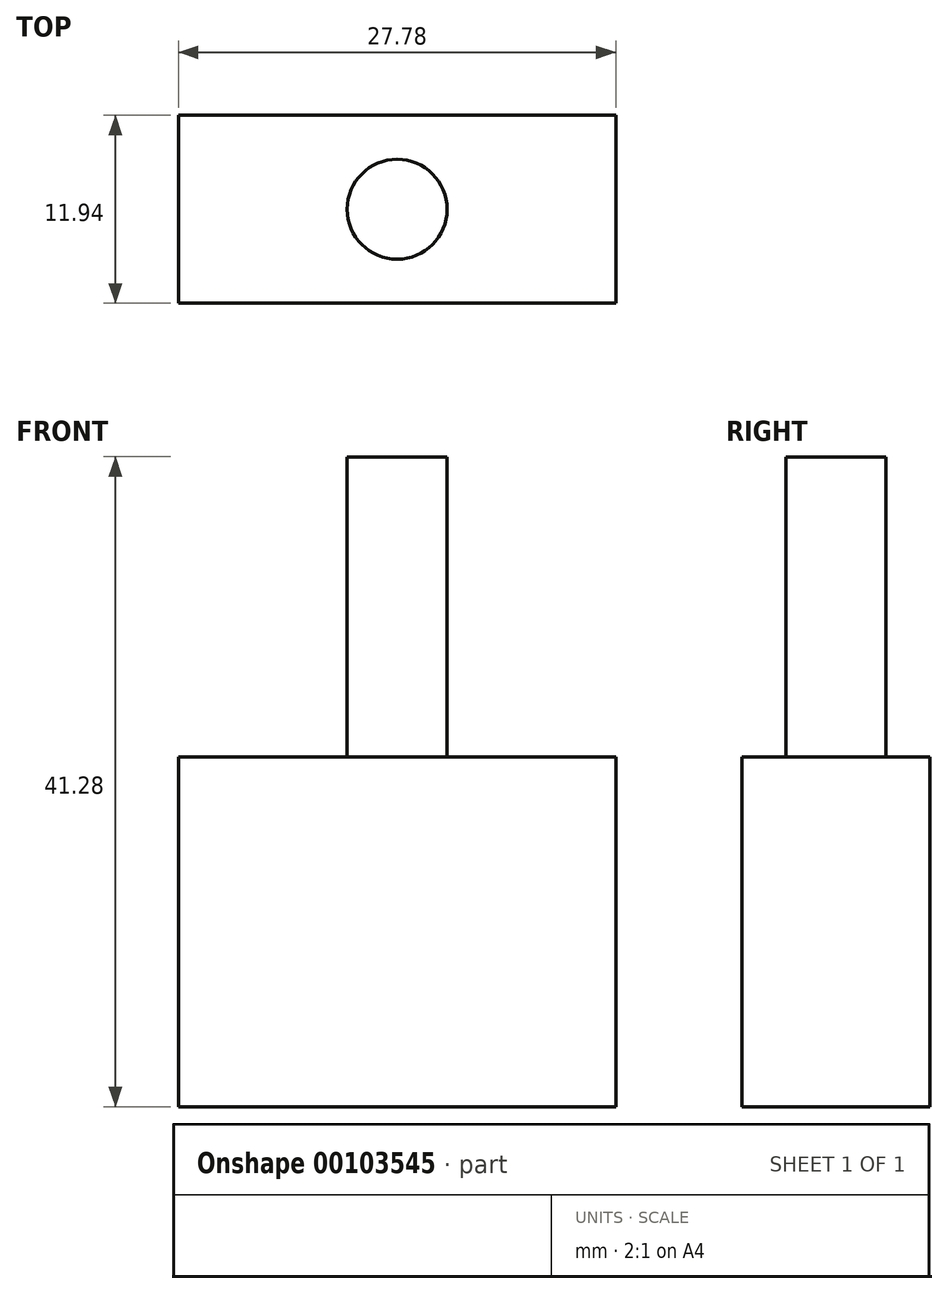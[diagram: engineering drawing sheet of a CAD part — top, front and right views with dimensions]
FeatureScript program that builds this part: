
annotation { "Feature Type Name" : "Feature", "Feature Type Description" : "" }
export const myFeature = defineFeature(function(context is Context, id is Id, definition is map)
    precondition{}
    {
        {
            var Q0;
            Q0=qCreatedBy(makeId("Front.planeOp"),FACE);
            var sketch = newSketch(context, id + "F0", { "sketchPlane" : qUnion([Q0])});
            skLineSegment(sketch, "E0.bottom", {"start": v(-23.1, 25.73) * mm, "end": v(4.67, 25.73) * mm});
            skLineSegment(sketch, "E0.top", {"start": v(-23.1, 3.5) * mm, "end": v(4.67, 3.5) * mm});
            skLineSegment(sketch, "E0.left", {"start": v(-23.1, 25.73) * mm, "end": v(-23.1, 3.5) * mm});
            skLineSegment(sketch, "E0.right", {"start": v(4.67, 25.73) * mm, "end": v(4.67, 3.5) * mm});
            skSolve(sketch);
        }
        {
            var Q0;
            Q0=qSketchRegion(id+"F0",true);
            extrude(context, id + "F1", {"entities" : qUnion([Q0]), "depth" : 11.94 * mm});
        }
        {
            var Q0;
            Q0=makeQuery(id+"F1.opExtrude","SWEPT_FACE",FACE,{"disambiguationData":[OSD([sQuery(id+"F0.wireOp",EDGE,"E0.bottom")])]});
            var sketch = newSketch(context, id + "F2", { "sketchPlane" : qUnion([Q0])});
            skCircle(sketch, "E1", {"center": v(-9.22, -5.97) * mm, "radius": 3.18 * mm});
            skPoint(sketch, "E1.centerSnap0", {"position": v(4.67, -5.97) * mm});
            skPoint(sketch, "E1.centerSnap1", {"position": v(-9.22, 0) * mm});
            skSolve(sketch);
        }
        {
            var Q0;
            Q0=makeQuery(id+"F2.imprint","IMPRINT",FACE,{"disambiguationData":[TD([[makeQuery(id+"F2.imprint","IMPRINT",EDGE,{"derivedFrom":sQuery(id+"F2.wireOp",EDGE,"E1")}),1.0]])]});
            extrude(context, id + "F3", {"entities" : qUnion([Q0]), "operationType" : NewBodyOperationType.ADD, "depth" : 19.05 * mm});
        }
    });
